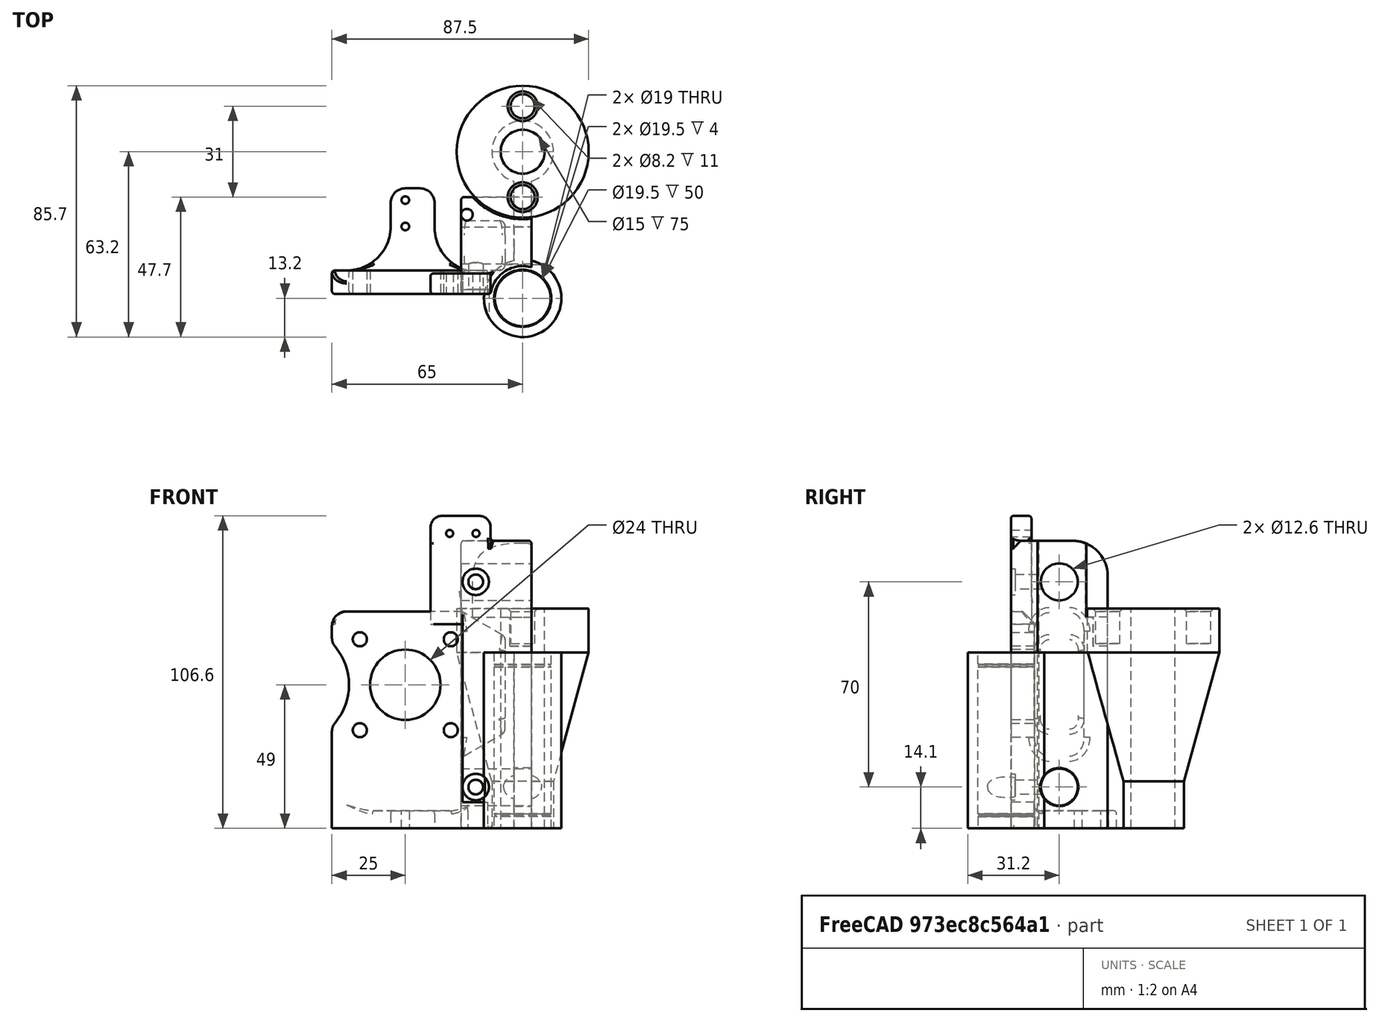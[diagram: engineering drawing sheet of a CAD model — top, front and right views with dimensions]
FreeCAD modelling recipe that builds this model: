
FCSTD DOCUMENT  (FreeCAD 0.16R6721 (Git))
Label: z_carriage_motor_v2.7
License: All rights reserved
LicenseURL: http://en.wikipedia.org/wiki/All_rights_reserved
objects: Part::FeaturePython×3, Sketcher::SketchObject×1, PartDesign::Pad×1, Part::Cut×1
note: 7 computed .brp shape members not serialized (recipe doc carries the construction recipe); baked Part::Feature solids carry a one-line shape summary decoded from their .brp

FEATURE [Part::FeaturePython] carriage_motor_mount_olive_01  # a2plus imported part (geometry in sourceFile) (typed FeaturePython)
  Placement = pos=(-40,-48.5,49) rot=(0.57735,0.57735,0.57735;4.18879rad)
  fixedPosition = false
  sourceFile = <userpath>/shared-j/devel/lulzbot/TAZ/Olive/production_parts/printed_parts/z_carriage_motor/carriage_motor_mount_olive.fcstd
  timeLastImport = 1458587576
  updateColors = true
FEATURE [Part::FeaturePython] carriage_motor_z_01  # a2plus imported part (geometry in sourceFile) (typed FeaturePython)
  Placement = pos=(3,-32,44.1) rot=(0.57735,-0.57735,-0.57735;2.0944rad)
  fixedPosition = false
  sourceFile = <userpath>/shared-j/devel/lulzbot/TAZ/Olive/production_parts/printed_parts/z_carriage_motor/carriage_motor_z.fcstd
  timeLastImport = 1460046477
  updateColors = true
FEATURE [Part::FeaturePython] carriage_base_olive_01  # a2plus imported part (geometry in sourceFile) (typed FeaturePython)
  Placement = pos=(0,0,0) rot=(1,0,0;1.5708rad)
  fixedPosition = false
  sourceFile = <userpath>/shared-j/devel/lulzbot/TAZ/Olive/production_parts/printed_parts/z_carriage_idler/carriage_base_olive.fcstd
  timeLastImport = 1460043793
  updateColors = true
FEATURE [Sketcher::SketchObject] Sketch
  Placement = pos=(0,-47,0) rot=(1,0,0;1.5708rad)
  sketch-geometry (1):
    g0: Circle CenterX=-16 CenterY=14.1 CenterZ=0 NormalX=0 NormalY=0 NormalZ=1 Radius=4.5
FEATURE [PartDesign::Pad] Pad
  Length = 10
  Length2 = 100
  Placement = pos=(0,-47,0) rot=(1,0,0;1.5708rad)
  Sketch = -> Sketch
  Type = 0
FEATURE [Part::Cut] Cut
  Base = -> carriage_base_olive_01
  Tool = -> Pad
